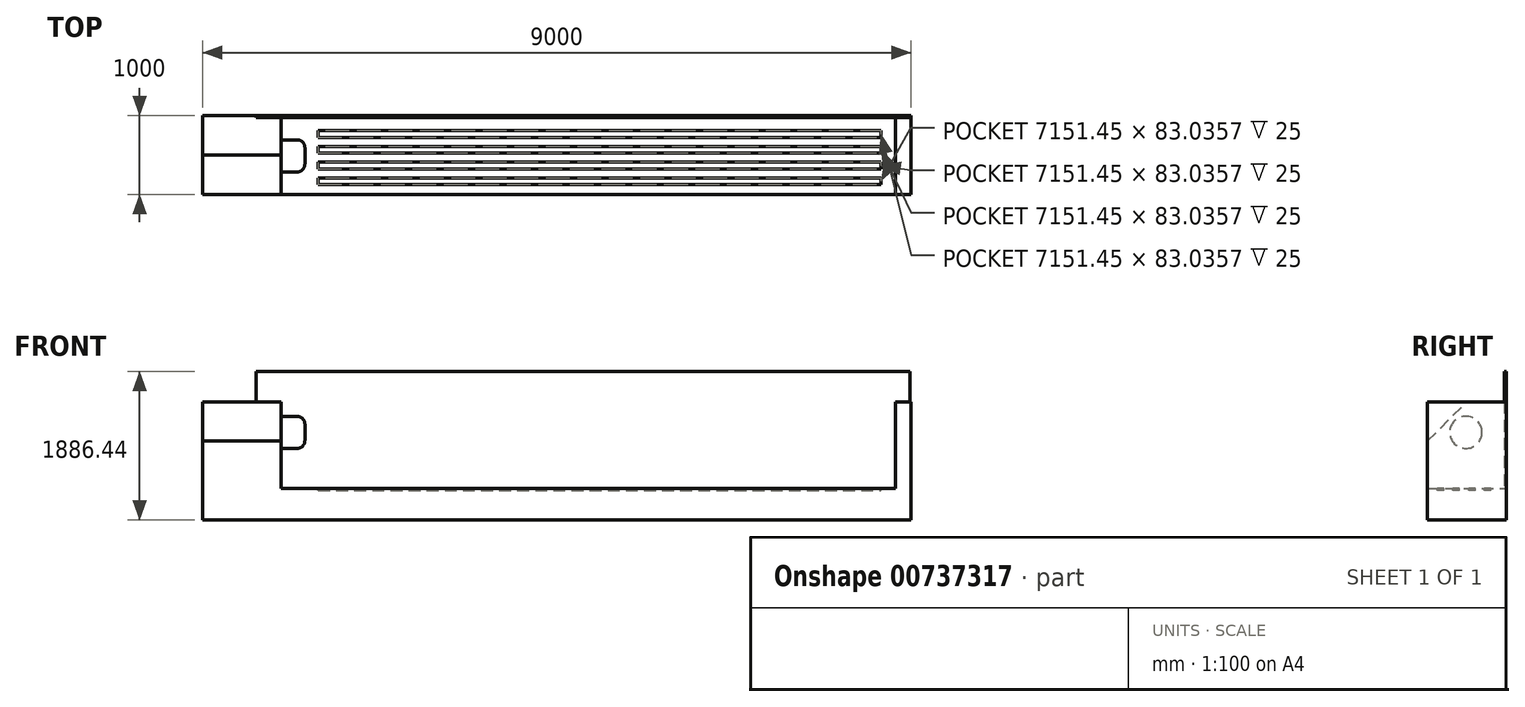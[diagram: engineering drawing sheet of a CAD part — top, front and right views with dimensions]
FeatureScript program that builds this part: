
annotation { "Feature Type Name" : "Feature", "Feature Type Description" : "" }
export const myFeature = defineFeature(function(context is Context, id is Id, definition is map)
    precondition{}
    {
        {
            var Q0;
            Q0=qCreatedBy(makeId("Front.planeOp"),FACE);
            var sketch = newSketch(context, id + "F0", { "sketchPlane" : qUnion([Q0])});
            skLineSegment(sketch, "E0", {"start": v(-2871.36, 1500) * mm, "end": v(-1871.36, 1500) * mm});
            skLineSegment(sketch, "E1", {"start": v(-1871.36, 1500) * mm, "end": v(-1871.36, 402.07) * mm});
            skLineSegment(sketch, "E2", {"start": v(-1871.36, 402.07) * mm, "end": v(5928.64, 402.07) * mm});
            skLineSegment(sketch, "E3", {"start": v(5928.64, 402.07) * mm, "end": v(5928.64, 1500) * mm});
            skLineSegment(sketch, "E4", {"start": v(5928.64, 1500) * mm, "end": v(6128.64, 1500) * mm});
            skLineSegment(sketch, "E5", {"start": v(6128.64, 1500) * mm, "end": v(6128.64, 0) * mm});
            skLineSegment(sketch, "E6", {"start": v(6128.64, 0) * mm, "end": v(-2871.36, 0) * mm});
            skLineSegment(sketch, "E7", {"start": v(-2871.36, 0) * mm, "end": v(-2871.36, 1500) * mm});
            skSolve(sketch);
        }
        {
            var Q0;
            Q0 = qSketchRegion(id + "F0", true);
            extrude(context, id + "F1", {"entities" : qUnion([Q0]), "depth" : 1000 * mm, "offsetDistance" : 25 * mm});
        }
        {
            var Q0;
            Q0=makeQuery(id+"F1.opExtrude","CAP_FACE",FACE,{"disambiguationData":[OSD([sQuery(id+"F0.wireOp",EDGE,"E0"),sQuery(id+"F0.wireOp",EDGE,"E1"),sQuery(id+"F0.wireOp",EDGE,"E2"),sQuery(id+"F0.wireOp",EDGE,"E3"),sQuery(id+"F0.wireOp",EDGE,"E4"),sQuery(id+"F0.wireOp",EDGE,"E5"),sQuery(id+"F0.wireOp",EDGE,"E6"),sQuery(id+"F0.wireOp",EDGE,"E7")])],"isStart":true});
            var sketch = newSketch(context, id + "F2", { "sketchPlane" : qUnion([Q0])});
            skLineSegment(sketch, "E8.bottom", {"start": v(-6115.63, 1886.44) * mm, "end": v(2192.15, 1886.44) * mm});
            skLineSegment(sketch, "E8.top", {"start": v(-6115.63, 240.56) * mm, "end": v(2192.15, 240.56) * mm});
            skLineSegment(sketch, "E8.left", {"start": v(-6115.63, 1886.44) * mm, "end": v(-6115.63, 240.56) * mm});
            skLineSegment(sketch, "E8.right", {"start": v(2192.15, 1886.44) * mm, "end": v(2192.15, 240.56) * mm});
            skSolve(sketch);
        }
        {
            var Q0;
            Q0 = qSketchRegion(id + "F2", true);
            extrude(context, id + "F3", {"entities" : qUnion([Q0]), "operationType" : NewBodyOperationType.ADD, "oppositeDirection" : true, "depth" : 25 * mm, "offsetDistance" : 25 * mm});
        }
        {
            var Q0;
            Q0=makeQuery(id+"F1.opExtrude","SWEPT_FACE",FACE,{"disambiguationData":[OSD([sQuery(id+"F0.wireOp",EDGE,"E1")])]});
            var sketch = newSketch(context, id + "F4", { "sketchPlane" : qUnion([Q0])});
            skCircle(sketch, "E9", {"center": v(-511.82, 1111.94) * mm, "radius": 204.27 * mm});
            skSolve(sketch);
        }
        {
            var Q0;
            Q0 = qSketchRegion(id + "F4", true);
            extrude(context, id + "F5", {"entities" : qUnion([Q0]), "operationType" : NewBodyOperationType.ADD, "depth" : 300 * mm, "offsetDistance" : 25 * mm});
        }
        {
            var Q0;
            Q0=makeQuery(id+"F1.opExtrude","CAP_EDGE",EDGE,{"disambiguationData":[OSD([sQuery(id+"F0.wireOp",EDGE,"E0")])],"isStart":false});
            chamfer(context, id + "F6", {"entities" : qUnion([Q0]), "width" : 500 * mm, "tangentPropagation" : true});
        }
        {
            var Q0;
            Q0=makeQuery(id+"F5.opExtrude","CAP_EDGE",EDGE,{"disambiguationData":[OSD([sQuery(id+"F4.wireOp",EDGE,"E9")])],"isStart":false});
            fillet(context, id + "F7", {"entities" : qUnion([Q0]), "radius" : 100 * mm, "tangentPropagation" : true, "allowEdgeOverflow" : false});
        }
        {
            var Q0;
            Q0=makeQuery(id+"F1.opExtrude","SWEPT_FACE",FACE,{"disambiguationData":[OSD([sQuery(id+"F0.wireOp",EDGE,"E2")])]});
            var sketch = newSketch(context, id + "F8", { "sketchPlane" : qUnion([Q0])});
            skLineSegment(sketch, "E10.bottom", {"start": v(-1402.97, -192.8) * mm, "end": v(5748.48, -192.8) * mm});
            skLineSegment(sketch, "E10.top", {"start": v(-1402.97, -275.83) * mm, "end": v(5748.48, -275.83) * mm});
            skLineSegment(sketch, "E10.left", {"start": v(-1402.97, -192.8) * mm, "end": v(-1402.97, -275.83) * mm});
            skLineSegment(sketch, "E10.right", {"start": v(5748.48, -192.8) * mm, "end": v(5748.48, -275.83) * mm});
            skLineSegment(sketch, "E11.0.1.0", {"start": v(-1402.97, -392.8) * mm, "end": v(5748.48, -392.8) * mm});
            skLineSegment(sketch, "E11.0.1.1", {"start": v(-1402.97, -475.83) * mm, "end": v(5748.48, -475.83) * mm});
            skLineSegment(sketch, "E11.0.1.2", {"start": v(-1402.97, -392.8) * mm, "end": v(-1402.97, -475.83) * mm});
            skLineSegment(sketch, "E11.0.1.3", {"start": v(5748.48, -392.8) * mm, "end": v(5748.48, -475.83) * mm});
            skLineSegment(sketch, "E11.0.2.0", {"start": v(-1402.97, -592.8) * mm, "end": v(5748.48, -592.8) * mm});
            skLineSegment(sketch, "E11.0.2.1", {"start": v(-1402.97, -675.83) * mm, "end": v(5748.48, -675.83) * mm});
            skLineSegment(sketch, "E11.0.2.2", {"start": v(-1402.97, -592.8) * mm, "end": v(-1402.97, -675.83) * mm});
            skLineSegment(sketch, "E11.0.2.3", {"start": v(5748.48, -592.8) * mm, "end": v(5748.48, -675.83) * mm});
            skLineSegment(sketch, "E11.direction1", {"start": v(-1402.97, -275.83) * mm, "end": v(-1202.97, -275.83) * mm, "construction": true});
            skLineSegment(sketch, "E11.direction2", {"start": v(-1402.97, -275.83) * mm, "end": v(-1402.97, -475.83) * mm, "construction": true});
            skLineSegment(sketch, "E12.0.0.3", {"start": v(-1402.97, -792.8) * mm, "end": v(5748.48, -792.8) * mm});
            skLineSegment(sketch, "E12.3.0.3", {"start": v(-1402.97, -875.83) * mm, "end": v(5748.48, -875.83) * mm});
            skLineSegment(sketch, "E12.6.0.3", {"start": v(-1402.97, -792.8) * mm, "end": v(-1402.97, -875.83) * mm});
            skLineSegment(sketch, "E12.9.0.3", {"start": v(5748.48, -792.8) * mm, "end": v(5748.48, -875.83) * mm});
            skSolve(sketch);
        }
        {
            var Q0;
            Q0 = qSketchRegion(id + "F8", true);
            extrude(context, id + "F9", {"entities" : qUnion([Q0]), "operationType" : NewBodyOperationType.REMOVE, "oppositeDirection" : true, "depth" : 25 * mm, "offsetDistance" : 25 * mm});
        }
    });
